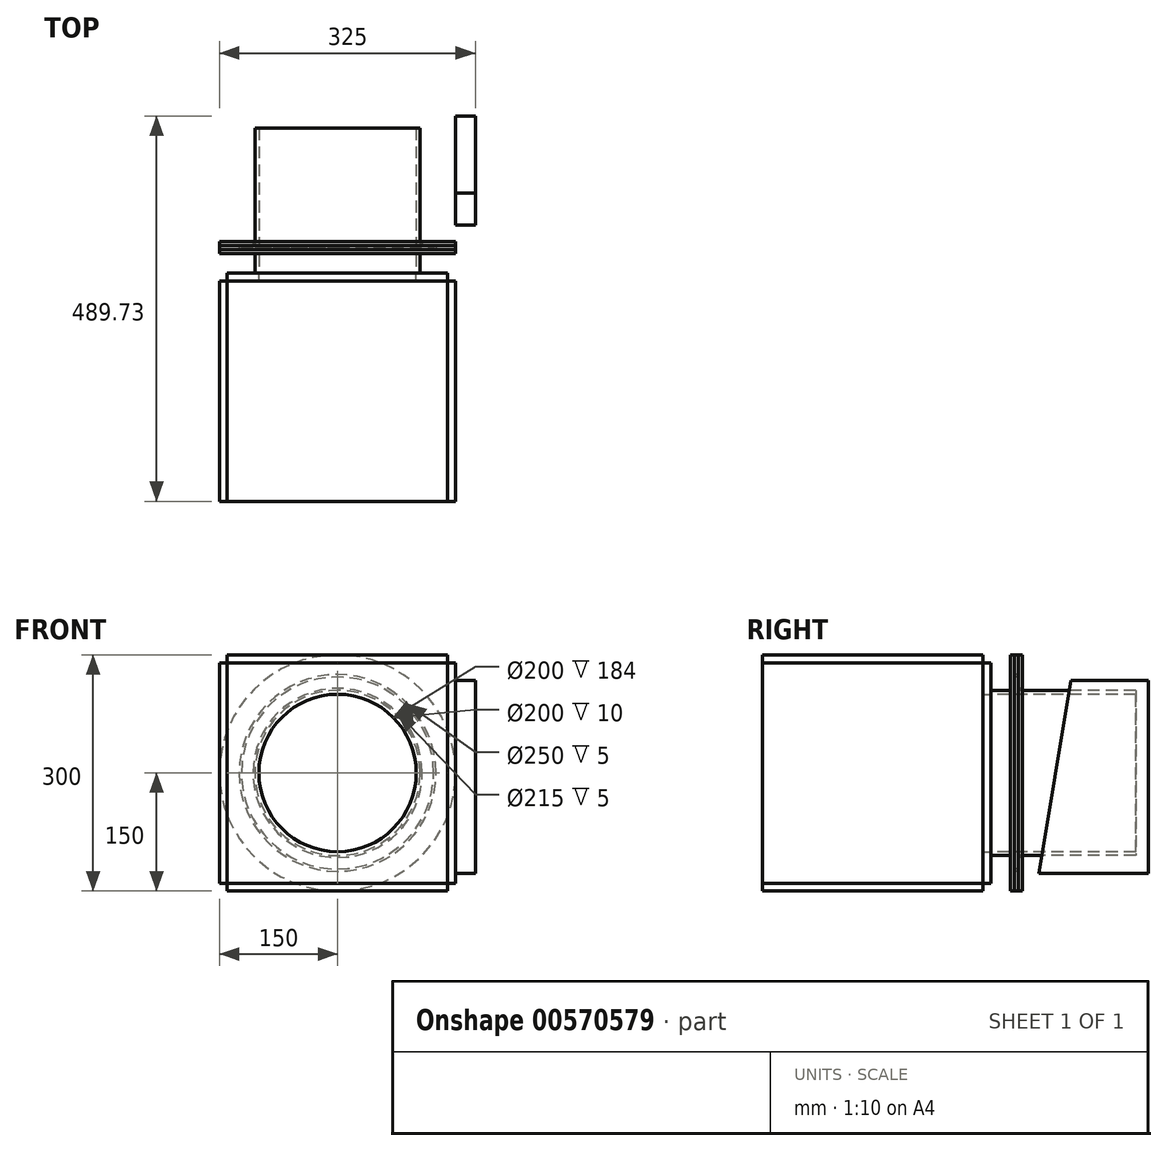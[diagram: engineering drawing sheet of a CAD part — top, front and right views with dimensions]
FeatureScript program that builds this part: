
annotation { "Feature Type Name" : "Feature", "Feature Type Description" : "" }
export const myFeature = defineFeature(function(context is Context, id is Id, definition is map)
    precondition{}
    {
        {
            var Q0;
            Q0=qCreatedBy(makeId("Front.planeOp"),FACE);
            var sketch = newSketch(context, id + "F0", { "sketchPlane" : qUnion([Q0])});
            skLineSegment(sketch, "E0.bottom", {"start": v(-140, 140) * mm, "end": v(140, 140) * mm});
            skLineSegment(sketch, "E0.top", {"start": v(-140, -140) * mm, "end": v(140, -140) * mm});
            skLineSegment(sketch, "E0.left", {"start": v(-140, 140) * mm, "end": v(-140, -140) * mm});
            skLineSegment(sketch, "E0.right", {"start": v(140, 140) * mm, "end": v(140, -140) * mm});
            skPoint(sketch, "E0.middle", {"position": v(0, 0) * mm});
            skCircle(sketch, "E1", {"center": v(0, 0) * mm, "radius": 100 * mm});
            skSolve(sketch);
        }
        {
            var Q0;
            Q0 = qSketchRegion(id + "F0", true);
            extrude(context, id + "F1", {"entities" : qUnion([Q0]), "depth" : 10 * mm, "offsetDistance" : 25 * mm});
        }
        {
            var Q0;
            Q0=makeQuery(id+"F1.opExtrude","CAP_FACE",FACE,{"disambiguationData":[OSD([sQuery(id+"F0.wireOp",EDGE,"E0.bottom"),sQuery(id+"F0.wireOp",EDGE,"E0.top"),sQuery(id+"F0.wireOp",EDGE,"E0.left"),sQuery(id+"F0.wireOp",EDGE,"E0.right"),sQuery(id+"F0.wireOp",EDGE,"E1")])],"isStart":false});
            var sketch = newSketch(context, id + "F2", { "sketchPlane" : qUnion([Q0])});
            skLineSegment(sketch, "E2.bottom", {"start": v(-140, 140) * mm, "end": v(140, 140) * mm});
            skLineSegment(sketch, "E2.top", {"start": v(-140, 150) * mm, "end": v(140, 150) * mm});
            skLineSegment(sketch, "E2.left", {"start": v(-140, 140) * mm, "end": v(-140, 150) * mm});
            skLineSegment(sketch, "E2.right", {"start": v(140, 140) * mm, "end": v(140, 150) * mm});
            skSolve(sketch);
        }
        {
            var Q0;
            Q0 = qSketchRegion(id + "F2", true);
            extrude(context, id + "F3", {"entities" : qUnion([Q0]), "depth" : 280 * mm, "offsetDistance" : 25 * mm});
        }
        {
            var Q0;
            Q0=makeQuery(id+"F1.opExtrude","CAP_FACE",FACE,{"disambiguationData":[OSD([sQuery(id+"F0.wireOp",EDGE,"E0.bottom"),sQuery(id+"F0.wireOp",EDGE,"E0.top"),sQuery(id+"F0.wireOp",EDGE,"E0.left"),sQuery(id+"F0.wireOp",EDGE,"E0.right"),sQuery(id+"F0.wireOp",EDGE,"E1")])],"isStart":false});
            var sketch = newSketch(context, id + "F4", { "sketchPlane" : qUnion([Q0])});
            skLineSegment(sketch, "E3.bottom", {"start": v(-140, 140) * mm, "end": v(-150, 140) * mm});
            skLineSegment(sketch, "E3.top", {"start": v(-140, -140) * mm, "end": v(-150, -140) * mm});
            skLineSegment(sketch, "E3.left", {"start": v(-140, 140) * mm, "end": v(-140, -140) * mm});
            skLineSegment(sketch, "E3.right", {"start": v(-150, 140) * mm, "end": v(-150, -140) * mm});
            skSolve(sketch);
        }
        {
            var Q0;
            Q0 = qSketchRegion(id + "F4", true);
            extrude(context, id + "F5", {"entities" : qUnion([Q0]), "depth" : 280 * mm, "offsetDistance" : 25 * mm});
        }
        {
            var Q0;
            Q0=makeQuery(id+"F1.opExtrude","CAP_FACE",FACE,{"disambiguationData":[OSD([sQuery(id+"F0.wireOp",EDGE,"E0.bottom"),sQuery(id+"F0.wireOp",EDGE,"E0.top"),sQuery(id+"F0.wireOp",EDGE,"E0.left"),sQuery(id+"F0.wireOp",EDGE,"E0.right"),sQuery(id+"F0.wireOp",EDGE,"E1")])],"isStart":false});
            var sketch = newSketch(context, id + "F6", { "sketchPlane" : qUnion([Q0])});
            skLineSegment(sketch, "E4.bottom", {"start": v(140, 140) * mm, "end": v(150, 140) * mm});
            skLineSegment(sketch, "E4.top", {"start": v(140, -140) * mm, "end": v(150, -140) * mm});
            skLineSegment(sketch, "E4.left", {"start": v(140, 140) * mm, "end": v(140, -140) * mm});
            skLineSegment(sketch, "E4.right", {"start": v(150, 140) * mm, "end": v(150, -140) * mm});
            skSolve(sketch);
        }
        {
            var Q0;
            Q0 = qSketchRegion(id + "F6", true);
            extrude(context, id + "F7", {"entities" : qUnion([Q0]), "depth" : 280 * mm, "offsetDistance" : 25 * mm});
        }
        {
            var Q0;
            Q0=makeQuery(id+"F1.opExtrude","CAP_FACE",FACE,{"disambiguationData":[OSD([sQuery(id+"F0.wireOp",EDGE,"E0.bottom"),sQuery(id+"F0.wireOp",EDGE,"E0.top"),sQuery(id+"F0.wireOp",EDGE,"E0.left"),sQuery(id+"F0.wireOp",EDGE,"E0.right"),sQuery(id+"F0.wireOp",EDGE,"E1")])],"isStart":false});
            var sketch = newSketch(context, id + "F8", { "sketchPlane" : qUnion([Q0])});
            skLineSegment(sketch, "E5.bottom", {"start": v(-140, -140) * mm, "end": v(140, -140) * mm});
            skLineSegment(sketch, "E5.top", {"start": v(-140, -150) * mm, "end": v(140, -150) * mm});
            skLineSegment(sketch, "E5.left", {"start": v(-140, -140) * mm, "end": v(-140, -150) * mm});
            skLineSegment(sketch, "E5.right", {"start": v(140, -140) * mm, "end": v(140, -150) * mm});
            skSolve(sketch);
        }
        {
            var Q0;
            Q0 = qSketchRegion(id + "F8", true);
            extrude(context, id + "F9", {"entities" : qUnion([Q0]), "depth" : 280 * mm, "offsetDistance" : 25 * mm});
        }
        {
            var Q0;
            Q0=makeQuery(id+"F1.opExtrude","CAP_FACE",FACE,{"disambiguationData":[OSD([sQuery(id+"F0.wireOp",EDGE,"E0.bottom"),sQuery(id+"F0.wireOp",EDGE,"E0.top"),sQuery(id+"F0.wireOp",EDGE,"E0.left"),sQuery(id+"F0.wireOp",EDGE,"E0.right"),sQuery(id+"F0.wireOp",EDGE,"E1")])],"isStart":true});
            var sketch = newSketch(context, id + "F10", { "sketchPlane" : qUnion([Q0])});
            skCircle(sketch, "E6", {"center": v(0, 0) * mm, "radius": 100 * mm});
            skCircle(sketch, "E7.0", {"center": v(0, 0) * mm, "radius": 105 * mm});
            skSolve(sketch);
        }
        {
            var Q0;
            Q0 = qSketchRegion(id + "F10", true);
            extrude(context, id + "F11", {"entities" : qUnion([Q0]), "depth" : 25 * mm, "offsetDistance" : 25 * mm});
        }
        {
            var Q0;
            Q0=makeQuery(id+"F11.opExtrude","CAP_FACE",FACE,{"disambiguationData":[OSD([sQuery(id+"F10.wireOp",EDGE,"E6"),sQuery(id+"F10.wireOp",EDGE,"E7.0")])],"isStart":false});
            var sketch = newSketch(context, id + "F12", { "sketchPlane" : qUnion([Q0])});
            skCircle(sketch, "E8", {"center": v(0, 0) * mm, "radius": 150 * mm});
            skCircle(sketch, "E9.0", {"center": v(0, 0) * mm, "radius": 100 * mm});
            skSolve(sketch);
        }
        {
            var Q0;
            Q0 = qSketchRegion(id + "F12", true);
            extrude(context, id + "F13", {"entities" : qUnion([Q0]), "operationType" : NewBodyOperationType.ADD, "depth" : 5 * mm, "offsetDistance" : 25 * mm});
        }
        {
            var Q0;
            Q0=makeQuery(id+"F13.opExtrude","CAP_FACE",FACE,{"disambiguationData":[OSD([sQuery(id+"F12.wireOp",EDGE,"E8"),sQuery(id+"F12.wireOp",EDGE,"E9.0")])],"isStart":false});
            var sketch = newSketch(context, id + "F14", { "sketchPlane" : qUnion([Q0])});
            skCircle(sketch, "E10", {"center": v(0, 0) * mm, "radius": 150 * mm});
            skCircle(sketch, "E11.0", {"center": v(0, 0) * mm, "radius": 125 * mm});
            skSolve(sketch);
        }
        {
            var Q0;
            Q0 = qSketchRegion(id + "F14", true);
            extrude(context, id + "F15", {"entities" : qUnion([Q0]), "depth" : 5 * mm, "offsetDistance" : 25 * mm});
        }
        {
            var Q0;
            Q0=makeQuery(id+"F13.opExtrude","CAP_FACE",FACE,{"disambiguationData":[OSD([sQuery(id+"F12.wireOp",EDGE,"E8"),sQuery(id+"F12.wireOp",EDGE,"E9.0")])],"isStart":false});
            var sketch = newSketch(context, id + "F16", { "sketchPlane" : qUnion([Q0])});
            skCircle(sketch, "E12", {"center": v(0, 0) * mm, "radius": 122 * mm});
            skCircle(sketch, "E13", {"center": v(0, 0) * mm, "radius": 100 * mm});
            skSolve(sketch);
        }
        {
            var Q0;
            Q0 = qSketchRegion(id + "F16", true);
            extrude(context, id + "F17", {"entities" : qUnion([Q0]), "operationType" : NewBodyOperationType.ADD, "depth" : 4 * mm, "offsetDistance" : 25 * mm});
        }
        {
            var Q0;
            Q0=makeQuery(id+"F17.opExtrude","CAP_FACE",FACE,{"disambiguationData":[OSD([sQuery(id+"F16.wireOp",EDGE,"E12"),sQuery(id+"F16.wireOp",EDGE,"E13")])],"isStart":false});
            var sketch = newSketch(context, id + "F18", { "sketchPlane" : qUnion([Q0])});
            skCircle(sketch, "E14", {"center": v(0, 0) * mm, "radius": 100 * mm});
            skCircle(sketch, "E15.0", {"center": v(0, 0) * mm, "radius": 105 * mm});
            skSolve(sketch);
        }
        {
            var Q0;
            Q0 = qSketchRegion(id + "F18", true);
            extrude(context, id + "F19", {"entities" : qUnion([Q0]), "operationType" : NewBodyOperationType.ADD, "depth" : 150 * mm, "offsetDistance" : 25 * mm});
        }
        {
            var Q0;
            Q0=makeQuery(id+"F15.opExtrude","CAP_FACE",FACE,{"disambiguationData":[OSD([sQuery(id+"F14.wireOp",EDGE,"E10"),sQuery(id+"F14.wireOp",EDGE,"E11.0")])],"isStart":false});
            var sketch = newSketch(context, id + "F20", { "sketchPlane" : qUnion([Q0])});
            skCircle(sketch, "E16", {"center": v(0, 0) * mm, "radius": 150 * mm});
            skCircle(sketch, "E17", {"center": v(0, 0) * mm, "radius": 107.5 * mm});
            skSolve(sketch);
        }
        {
            var Q0;
            Q0 = qSketchRegion(id + "F20", true);
            extrude(context, id + "F21", {"entities" : qUnion([Q0]), "depth" : 5 * mm, "offsetDistance" : 25 * mm});
        }
        {
            var Q0;
            Q0=makeQuery(id+"F7.opExtrude","SWEPT_FACE",FACE,{"disambiguationData":[OSD([sQuery(id+"F6.wireOp",EDGE,"E4.right")])]});
            var sketch = newSketch(context, id + "F22", { "sketchPlane" : qUnion([Q0])});
            skLineSegment(sketch, "E18", {"start": v(101.75, 117.67) * mm, "end": v(199.73, 117.67) * mm});
            skLineSegment(sketch, "E19", {"start": v(199.73, 117.67) * mm, "end": v(199.73, -127.28) * mm});
            skLineSegment(sketch, "E20", {"start": v(199.73, -127.28) * mm, "end": v(61, -127.28) * mm});
            skLineSegment(sketch, "E21", {"start": v(61, -127.28) * mm, "end": v(101.75, 117.67) * mm});
            skSolve(sketch);
        }
        {
            var Q0;
            Q0 = qSketchRegion(id + "F22", true);
            extrude(context, id + "F23", {"entities" : qUnion([Q0]), "depth" : 25 * mm, "offsetDistance" : 25 * mm});
        }
    });
